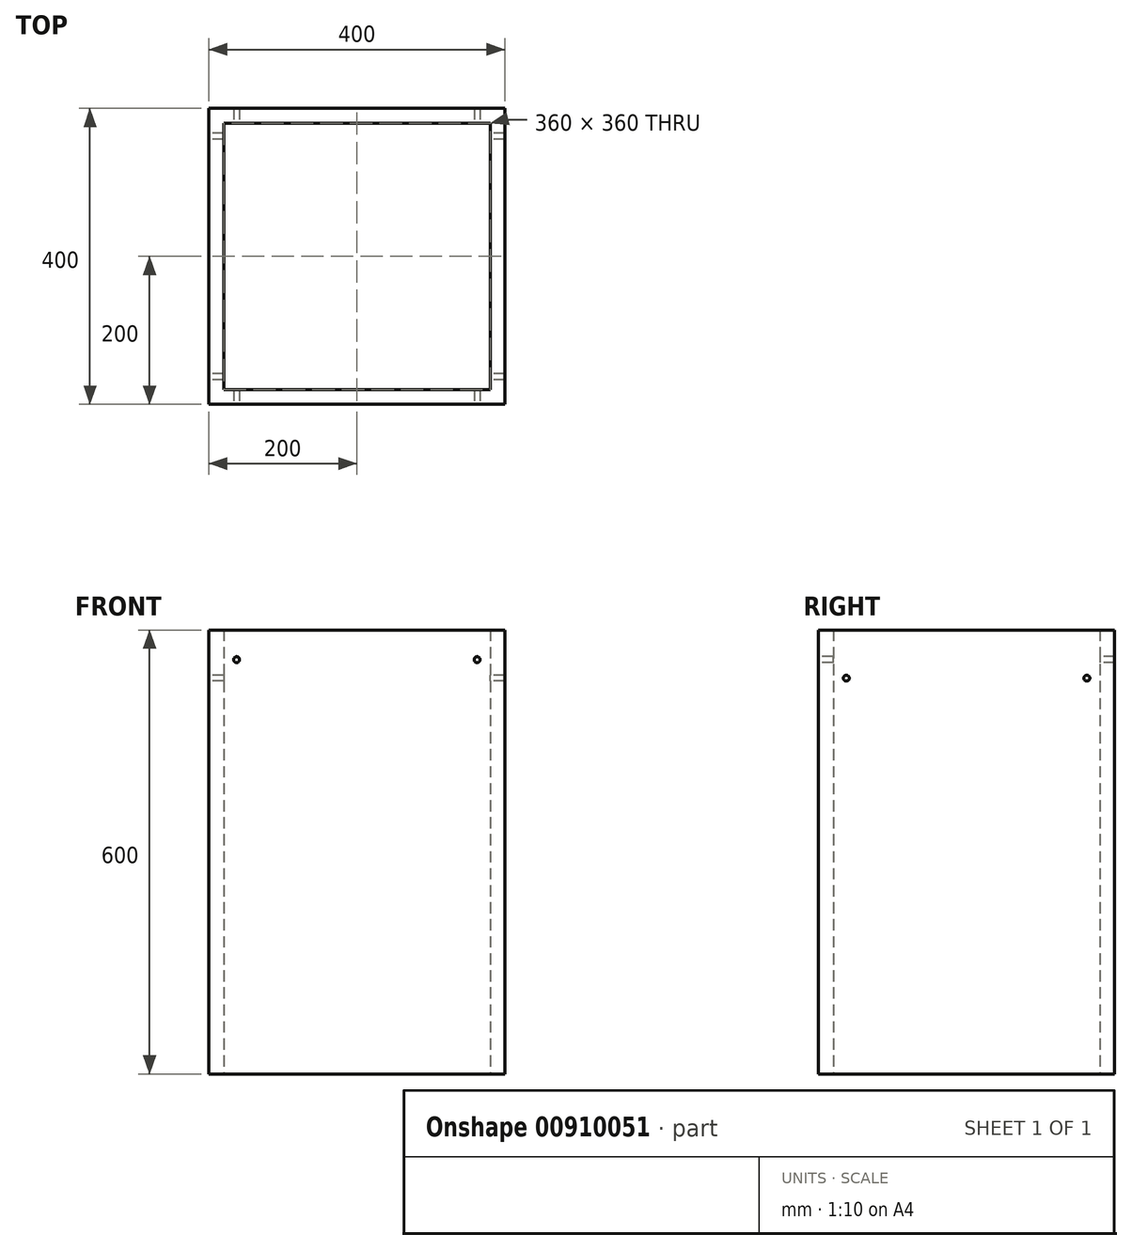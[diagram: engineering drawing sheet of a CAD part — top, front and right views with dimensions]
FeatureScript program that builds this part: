
annotation { "Feature Type Name" : "Feature", "Feature Type Description" : "" }
export const myFeature = defineFeature(function(context is Context, id is Id, definition is map)
    precondition{}
    {
        {
            var Q0;
            Q0=qCreatedBy(makeId("Top.planeOp"),FACE);
            var sketch = newSketch(context, id + "F0", { "sketchPlane" : qUnion([Q0])});
            skLineSegment(sketch, "E0.bottom", {"start": v(0, 0) * mm, "end": v(400, 0) * mm});
            skLineSegment(sketch, "E0.top", {"start": v(0, 400) * mm, "end": v(400, 400) * mm});
            skLineSegment(sketch, "E0.left", {"start": v(0, 0) * mm, "end": v(0, 400) * mm});
            skLineSegment(sketch, "E0.right", {"start": v(400, 0) * mm, "end": v(400, 400) * mm});
            skLineSegment(sketch, "E1", {"start": v(0, 0) * mm, "end": v(20, 0) * mm});
            skLineSegment(sketch, "E2", {"start": v(20, 0) * mm, "end": v(20, 380) * mm});
            skLineSegment(sketch, "E3", {"start": v(20, 380) * mm, "end": v(380, 380) * mm});
            skLineSegment(sketch, "E4", {"start": v(380, 380) * mm, "end": v(380, 20) * mm});
            skLineSegment(sketch, "E5", {"start": v(380, 20) * mm, "end": v(20, 20) * mm});
            skSolve(sketch);
        }
        {
            var Q0;
            Q0=makeQuery(id+"F0.imprint","IMPRINT",FACE,{"disambiguationData":[TD([[makeQuery(id+"F0.imprint","IMPRINT",EDGE,{"derivedFrom":sQuery(id+"F0.wireOp",EDGE,"E0.top")}),-1.0]])]});
            extrude(context, id + "F1", {"entities" : qUnion([Q0]), "depth" : 600 * mm, "offsetDistance" : 25 * mm});
        }
        {
            var Q0;
            Q0=makeQuery(id+"F1.opExtrude","SWEPT_FACE",FACE,{"disambiguationData":[OSD([sQuery(id+"F0.wireOp",EDGE,"E0.bottom")])]});
            var sketch = newSketch(context, id + "F2", { "sketchPlane" : qUnion([Q0])});
            skLineSegment(sketch, "E6", {"start": v(200, 600) * mm, "end": v(200, 560) * mm});
            skLineSegment(sketch, "E7", {"start": v(200, 560) * mm, "end": v(37.5, 560) * mm});
            skLineSegment(sketch, "E8", {"start": v(200, 560) * mm, "end": v(362.5, 560) * mm});
            skCircle(sketch, "E9", {"center": v(37.5, 560) * mm, "radius": 4 * mm});
            skCircle(sketch, "E10", {"center": v(362.5, 560) * mm, "radius": 4 * mm});
            skSolve(sketch);
        }
        {
            var Q0;
            Q0=makeQuery(id+"F2.imprint","IMPRINT",FACE,{"disambiguationData":[TD([[makeQuery(id+"F2.imprint","IMPRINT",EDGE,{"derivedFrom":sQuery(id+"F2.wireOp",EDGE,"E9")}),1.0]])]});
            var Q1;
            Q1=makeQuery(id+"F2.imprint","IMPRINT",FACE,{"disambiguationData":[TD([[makeQuery(id+"F2.imprint","IMPRINT",EDGE,{"derivedFrom":sQuery(id+"F2.wireOp",EDGE,"E10")}),1.0]])]});
            extrude(context, id + "F3", {"entities" : qUnion([Q0, Q1]), "operationType" : NewBodyOperationType.REMOVE, "oppositeDirection" : true, "depth" : 406 * mm, "offsetDistance" : 25 * mm});
        }
        {
            var Q0;
            Q0=makeQuery(id+"F1.opExtrude","SWEPT_FACE",FACE,{"disambiguationData":[OSD([sQuery(id+"F0.wireOp",EDGE,"E0.left")])]});
            var sketch = newSketch(context, id + "F4", { "sketchPlane" : qUnion([Q0])});
            skLineSegment(sketch, "E11", {"start": v(-200, 600) * mm, "end": v(-200, 535) * mm});
            skLineSegment(sketch, "E12", {"start": v(-200, 535) * mm, "end": v(-362.5, 535) * mm});
            skLineSegment(sketch, "E13", {"start": v(-200, 535) * mm, "end": v(-37.5, 535) * mm});
            skCircle(sketch, "E14", {"center": v(-362.5, 535) * mm, "radius": 4 * mm});
            skCircle(sketch, "E15", {"center": v(-37.5, 535) * mm, "radius": 4 * mm});
            skSolve(sketch);
        }
        {
            var Q0;
            Q0=makeQuery(id+"F4.imprint","IMPRINT",FACE,{"disambiguationData":[TD([[makeQuery(id+"F4.imprint","IMPRINT",EDGE,{"derivedFrom":sQuery(id+"F4.wireOp",EDGE,"E14")}),1.0]])]});
            var Q1;
            Q1=makeQuery(id+"F4.imprint","IMPRINT",FACE,{"disambiguationData":[TD([[makeQuery(id+"F4.imprint","IMPRINT",EDGE,{"derivedFrom":sQuery(id+"F4.wireOp",EDGE,"E15")}),1.0]])]});
            extrude(context, id + "F5", {"entities" : qUnion([Q0, Q1]), "operationType" : NewBodyOperationType.REMOVE, "oppositeDirection" : true, "depth" : 467 * mm, "offsetDistance" : 25 * mm});
        }
    });
